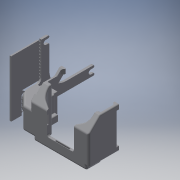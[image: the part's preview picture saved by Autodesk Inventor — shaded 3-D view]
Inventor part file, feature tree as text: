
AUTODESK INVENTOR PART (.ipt)
format: ipt  version: 2016 (Build 200138000, 138)  size: 1,237,504 bytes
history: native  units: in
note: dims shown in document units (in); Inventor stores cm internally (conversion verified against a paired STEP export)
features: extrude x8, sketch x8, fillet x5, other x1, plane x1, pattern_linear x1, imported_body x1
ambient origin geometry x8: Origin, YZ Plane, XZ Plane, XY Plane, X Axis, Y Axis, Z Axis, Center Point
bodies: Solid1 (feature_tree)
feature tree (25):
  other  "uploads-a6-b2-57-75-86-ReplicatorFanDuct21"
  extrude  "Extrusion1"  Depth=0.1in TaperAngle=0.0deg
  fillet  "Fillet1"  Radius=0.1969in
  extrude  "Extrusion2"  Depth=1.3126in
  fillet  "Fillet2"  Radius=0.1in
  extrude  "Extrusion4"  Depth=0.1575in
  fillet  "Fillet3"  Radius=1.5748in
  extrude  "Extrusion5"  Depth=0.0787in
  fillet  "Fillet4"  Radius=0.1575in
  fillet  "Fillet5"  Radius=0.0787in
  plane  "Work Plane1"
  extrude  "Extrusion7"  Depth=0.0787in
  extrude  "Extrusion8"  Depth=0.1969in
  pattern_linear  "Rectangular Pattern1"  Spacing1=0.0394in  [1 undecoded]
  extrude  "Extrusion9"  Depth=0.0591in
  extrude  "Extrusion10"  Depth=0.0984in
  imported_body  "Base1"
  sketch  "Sketch1"  dims[d0=0.4331in d1=0.1in d2=0.0in d3=0.1969in]
  sketch  "Sketch2"  dims[d4=0.2756in d5=1.3126in d6=0.1in d7=0.0in]
  sketch  "Sketch4"  dims[d8=0.1575in d13=0.315in d14=1.5748in]
  sketch  "Sketch6"  dims[d15=0.1in d16=0.0in d17=0.5906in d19=0.1575in d20=0.0787in]
  sketch  "Sketch8"  dims[d21=0.0787in d22=0.0787in]
  sketch  "Sketch9"  dims[d23=0.1969in d24=0.1969in]
  sketch  "Sketch10"  dims[d25=0.1in d26=0.0in]
  sketch  "Sketch11"  dims[d27=0.0394in d28=0.0394in d34=0.0591in d35=0.0984in d36=0.0591in d37=0.05in d38=0.0in d39=0.05in d40=0.0in d41=4.7244in d43=0.0984in d44=1.1811in d46=0.1181in d47=0.3937in d49=0.3937in d51=0.05in d52=0.0in d53=0.05in d54=0.0in]
note: 1 required parameter value undecoded (feature->parameter linkage not recoverable at this tier; creation-order binding heuristic only, values carry confidence <= 0.55)
